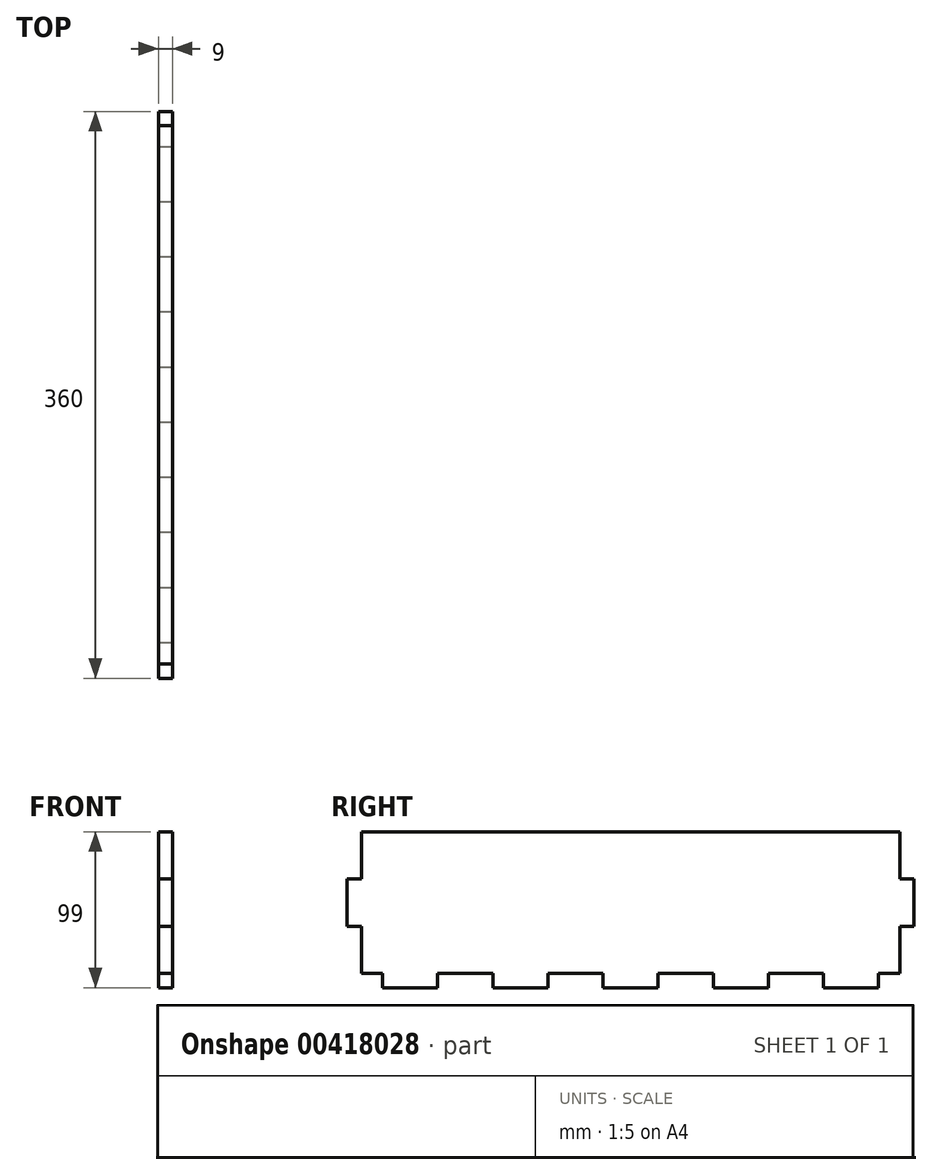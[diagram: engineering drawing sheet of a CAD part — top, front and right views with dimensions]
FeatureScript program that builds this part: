
annotation { "Feature Type Name" : "Feature", "Feature Type Description" : "" }
export const myFeature = defineFeature(function(context is Context, id is Id, definition is map)
    precondition{}
    {
        {
            var Q0;
            Q0=qCreatedBy(makeId("Right.planeOp"),FACE);
            var sketch = newSketch(context, id + "F0", { "sketchPlane" : qUnion([Q0])});
            skLineSegment(sketch, "E0.bottom", {"start": v(-180, 0) * mm, "end": v(180, 0) * mm, "construction": true});
            skLineSegment(sketch, "E0.top", {"start": v(-180, 90) * mm, "end": v(180, 90) * mm, "construction": true});
            skLineSegment(sketch, "E0.left", {"start": v(-180, 0) * mm, "end": v(-180, 90) * mm, "construction": true});
            skLineSegment(sketch, "E0.right", {"start": v(180, 0) * mm, "end": v(180, 90) * mm, "construction": true});
            skLineSegment(sketch, "E1.top", {"start": v(-180, -9) * mm, "end": v(180, -9) * mm, "construction": true});
            skLineSegment(sketch, "E1.left", {"start": v(-180, 0) * mm, "end": v(-180, -9) * mm, "construction": true});
            skLineSegment(sketch, "E1.right", {"start": v(180, 0) * mm, "end": v(180, -9) * mm, "construction": true});
            skLineSegment(sketch, "E2", {"start": v(-171, 90) * mm, "end": v(-171, 0) * mm, "construction": true});
            skLineSegment(sketch, "E3", {"start": v(-180, 60) * mm, "end": v(-171, 60) * mm});
            skLineSegment(sketch, "E4", {"start": v(-171, 60) * mm, "end": v(-171, 90) * mm});
            skLineSegment(sketch, "E5", {"start": v(-171, 90) * mm, "end": v(0, 90) * mm});
            skLineSegment(sketch, "E6", {"start": v(-180, 60) * mm, "end": v(-180, 30) * mm});
            skLineSegment(sketch, "E7", {"start": v(-180, 30) * mm, "end": v(-171, 30) * mm});
            skLineSegment(sketch, "E8", {"start": v(-171, 30) * mm, "end": v(-171, 0) * mm});
            skLineSegment(sketch, "E9", {"start": v(-171, 0) * mm, "end": v(-157.5, 0) * mm});
            skLineSegment(sketch, "E10", {"start": v(-157.5, 0) * mm, "end": v(-157.5, -9) * mm});
            skLineSegment(sketch, "E11", {"start": v(-157.5, -9) * mm, "end": v(-122.5, -9) * mm});
            skLineSegment(sketch, "E12", {"start": v(-122.5, -9) * mm, "end": v(-122.5, 0) * mm});
            skLineSegment(sketch, "E13", {"start": v(-122.5, 0) * mm, "end": v(-87.5, 0) * mm});
            skLineSegment(sketch, "E14", {"start": v(-87.5, 0) * mm, "end": v(-87.5, -9) * mm});
            skLineSegment(sketch, "E15", {"start": v(-87.5, -9) * mm, "end": v(-52.5, -9) * mm});
            skLineSegment(sketch, "E16", {"start": v(-52.5, -9) * mm, "end": v(-52.5, 0) * mm});
            skLineSegment(sketch, "E17", {"start": v(-52.5, 0) * mm, "end": v(-17.5, 0) * mm});
            skLineSegment(sketch, "E18", {"start": v(-17.5, 0) * mm, "end": v(-17.5, -9) * mm});
            skLineSegment(sketch, "E19", {"start": v(-17.5, -9) * mm, "end": v(0, -9) * mm});
            skLineSegment(sketch, "E20.MirrorCS", {"start": v(171, 90) * mm, "end": v(0, 90) * mm});
            skLineSegment(sketch, "E21.MirrorCS", {"start": v(171, 60) * mm, "end": v(171, 90) * mm});
            skLineSegment(sketch, "E22.MirrorCS", {"start": v(180, 60) * mm, "end": v(171, 60) * mm});
            skLineSegment(sketch, "E23.MirrorCS", {"start": v(180, 60) * mm, "end": v(180, 30) * mm});
            skLineSegment(sketch, "E24.MirrorCS", {"start": v(180, 30) * mm, "end": v(171, 30) * mm});
            skLineSegment(sketch, "E25.MirrorCS", {"start": v(171, 30) * mm, "end": v(171, 0) * mm});
            skLineSegment(sketch, "E26.MirrorCS", {"start": v(171, 0) * mm, "end": v(157.5, 0) * mm});
            skLineSegment(sketch, "E27.MirrorCS", {"start": v(157.5, -9) * mm, "end": v(122.5, -9) * mm});
            skLineSegment(sketch, "E28.MirrorCS", {"start": v(122.5, -9) * mm, "end": v(122.5, 0) * mm});
            skLineSegment(sketch, "E29.MirrorCS", {"start": v(122.5, 0) * mm, "end": v(87.5, 0) * mm});
            skLineSegment(sketch, "E30.MirrorCS", {"start": v(87.5, 0) * mm, "end": v(87.5, -9) * mm});
            skLineSegment(sketch, "E31.MirrorCS", {"start": v(87.5, -9) * mm, "end": v(52.5, -9) * mm});
            skLineSegment(sketch, "E32.MirrorCS", {"start": v(52.5, -9) * mm, "end": v(52.5, 0) * mm});
            skLineSegment(sketch, "E33.MirrorCS", {"start": v(52.5, 0) * mm, "end": v(17.5, 0) * mm});
            skLineSegment(sketch, "E34.MirrorCS", {"start": v(17.5, 0) * mm, "end": v(17.5, -9) * mm});
            skLineSegment(sketch, "E35.MirrorCS", {"start": v(17.5, -9) * mm, "end": v(0, -9) * mm});
            skLineSegment(sketch, "E36.MirrorCS", {"start": v(157.5, 0) * mm, "end": v(157.5, -9) * mm});
            skSolve(sketch);
        }
        {
            var Q0;
            Q0 = qSketchRegion(id + "F0", true);
            extrude(context, id + "F1", {"entities" : qUnion([Q0]), "depth" : 9 * mm});
        }
    });
